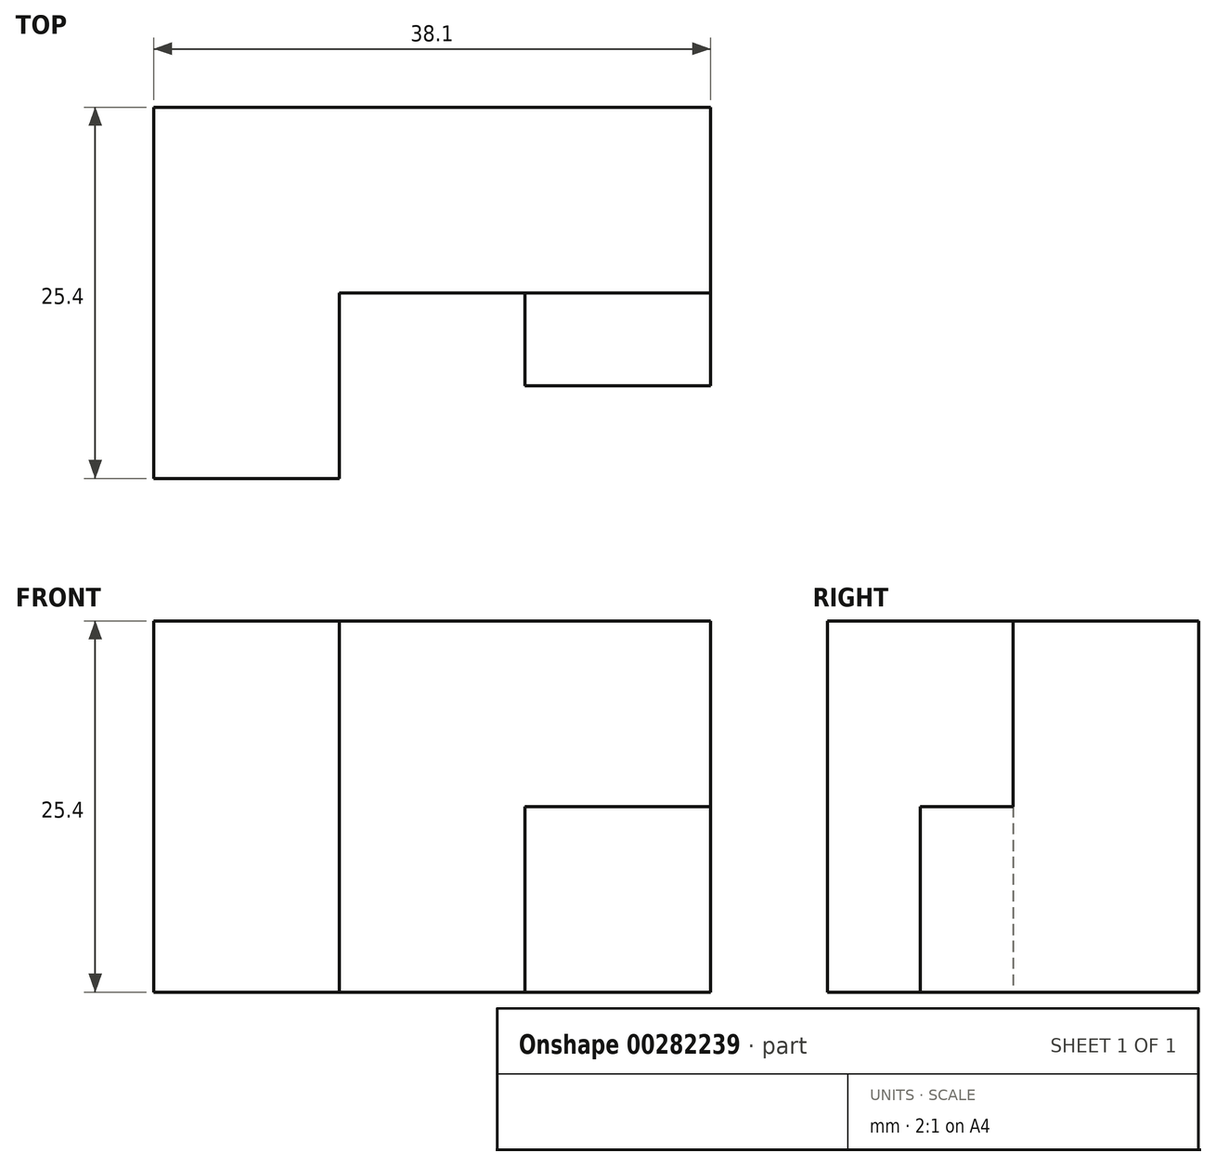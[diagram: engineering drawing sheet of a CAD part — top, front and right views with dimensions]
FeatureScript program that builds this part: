
annotation { "Feature Type Name" : "Feature", "Feature Type Description" : "" }
export const myFeature = defineFeature(function(context is Context, id is Id, definition is map)
    precondition{}
    {
        {
            var Q0;
            Q0=qCreatedBy(makeId("Front.planeOp"),FACE);
            var sketch = newSketch(context, id + "F0", { "sketchPlane" : qUnion([Q0])});
            skLineSegment(sketch, "E0.bottom", {"start": v(0, 0) * mm, "end": v(12.7, 0) * mm});
            skLineSegment(sketch, "E0.top", {"start": v(0, 25.4) * mm, "end": v(12.7, 25.4) * mm});
            skLineSegment(sketch, "E0.left", {"start": v(0, 0) * mm, "end": v(0, 25.4) * mm});
            skLineSegment(sketch, "E0.right", {"start": v(12.7, 0) * mm, "end": v(12.7, 25.4) * mm});
            skSolve(sketch);
        }
        {
            var Q0;
            Q0=makeQuery(id+"F0.imprint","IMPRINT",FACE,{"disambiguationData":[TD([[makeQuery(id+"F0.imprint","IMPRINT",EDGE,{"derivedFrom":sQuery(id+"F0.wireOp",EDGE,"E0.bottom")}),1.0]])]});
            extrude(context, id + "F1", {"entities" : qUnion([Q0]), "oppositeDirection" : true, "depth" : 25.4 * mm});
        }
        {
            var Q0;
            Q0=makeQuery(id+"F1.opExtrude","SWEPT_FACE",FACE,{"disambiguationData":[OSD([sQuery(id+"F0.wireOp",EDGE,"E0.right")])]});
            var sketch = newSketch(context, id + "F2", { "sketchPlane" : qUnion([Q0])});
            skLineSegment(sketch, "E1.bottom", {"start": v(12.7, 25.4) * mm, "end": v(25.4, 25.4) * mm});
            skLineSegment(sketch, "E1.top", {"start": v(12.7, 0) * mm, "end": v(25.4, 0) * mm});
            skLineSegment(sketch, "E1.left", {"start": v(12.7, 25.4) * mm, "end": v(12.7, 0) * mm});
            skLineSegment(sketch, "E1.right", {"start": v(25.4, 25.4) * mm, "end": v(25.4, 0) * mm});
            skSolve(sketch);
        }
        {
            var Q0;
            Q0=makeQuery(id+"F2.imprint","IMPRINT",FACE,{"disambiguationData":[TD([[makeQuery(id+"F2.imprint","IMPRINT",EDGE,{"derivedFrom":sQuery(id+"F2.wireOp",EDGE,"E1.bottom")}),1.0]])]});
            extrude(context, id + "F3", {"entities" : qUnion([Q0]), "operationType" : NewBodyOperationType.ADD, "depth" : 25.4 * mm});
        }
        {
            var Q0;
            Q0=makeQuery(id+"F3.opExtrude","SWEPT_FACE",FACE,{"disambiguationData":[OSD([sQuery(id+"F2.wireOp",EDGE,"E1.left")])]});
            var sketch = newSketch(context, id + "F4", { "sketchPlane" : qUnion([Q0])});
            skLineSegment(sketch, "E2.bottom", {"start": v(38.1, 0) * mm, "end": v(25.4, 0) * mm});
            skLineSegment(sketch, "E2.top", {"start": v(38.1, 12.7) * mm, "end": v(25.4, 12.7) * mm});
            skLineSegment(sketch, "E2.left", {"start": v(38.1, 0) * mm, "end": v(38.1, 12.7) * mm});
            skLineSegment(sketch, "E2.right", {"start": v(25.4, 0) * mm, "end": v(25.4, 12.7) * mm});
            skSolve(sketch);
        }
        {
            var Q0;
            Q0=makeQuery(id+"F4.imprint","IMPRINT",FACE,{"disambiguationData":[TD([[makeQuery(id+"F4.imprint","IMPRINT",EDGE,{"derivedFrom":sQuery(id+"F4.wireOp",EDGE,"E2.bottom")}),-1.0]])]});
            extrude(context, id + "F5", {"entities" : qUnion([Q0]), "operationType" : NewBodyOperationType.ADD, "depth" : 6.35 * mm});
        }
    });
